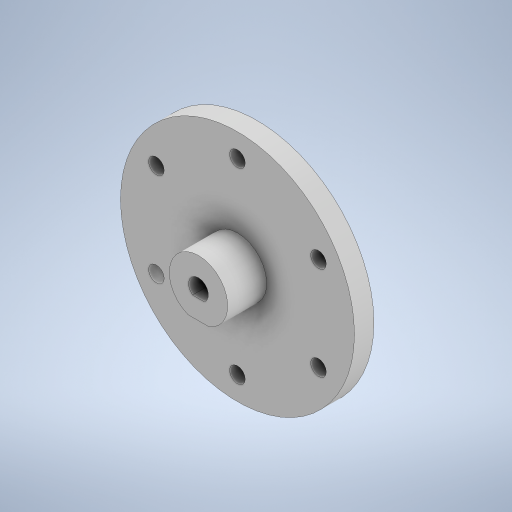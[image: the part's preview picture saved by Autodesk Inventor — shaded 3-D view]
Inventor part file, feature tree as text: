
AUTODESK INVENTOR PART (.ipt)
format: ipt  version: 2024 (Build 280153000, 153)  size: 319,488 bytes
history: native  units: mm
features: extrude x9, sketch x9
ambient origin geometry x8: Origin, YZ Plane, XZ Plane, XY Plane, X Axis, Y Axis, Z Axis, Center Point
bodies: Body1 (feature_tree)
feature tree (18):
  extrude  "Extrusion2"  Depth=5.0mm TaperAngle=0.0deg
  extrude  "Extrusion3"  Depth=7.0mm TaperAngle=0.0deg
  extrude  "Extrusion4"  Depth=10.0mm TaperAngle=0.0deg
  extrude  "Extrusion5"  Depth=4.6mm
  extrude  "Extrusion6"  Depth=2.0mm
  extrude  "Extrusion7"  Depth=20.0mm TaperAngle=0.0deg
  extrude  "Extrusion8"  Depth=10.0mm TaperAngle=0.0deg
  extrude  "Extrusion9"  Depth=24.0mm
  extrude  "Extrusion10"  Depth=7.5mm
  sketch  "Skizze2"  dims[d3=60.0mm d4=5.0mm d5=0.0mm]
  sketch  "Skizze3"  dims[d6=21.0mm d7=7.0mm d8=0.0mm]
  sketch  "Skizze4"  dims[d9=15.0mm d10=10.0mm d11=0.0mm]
  sketch  "Skizze5"  dims[d12=5.1mm d14=4.6mm]
  sketch  "Skizze6"  dims[d15=20.0mm d16=0.0mm d17=2.0mm]
  sketch  "Skizze7"  dims[d20=5.0mm d21=20.0mm d22=0.0mm]
  sketch  "Skizze8"  dims[d23=7.0mm d24=10.0mm d25=0.0mm]
  sketch  "Skizze9"  dims[d26=48.0mm d27=24.0mm]
  sketch  "Skizze11"  dims[d28=4.0mm d29=4.0mm d30=4.0mm d31=4.0mm d32=4.0mm d33=4.0mm d34=20.0mm d35=0.0mm d36=17.0mm d37=7.5mm d38=0.0mm d47=4.0mm d48=50.0mm d49=0.0mm d40=0.5mm d41=0.872665mm d42=0.5mm d43=0.872665mm]
